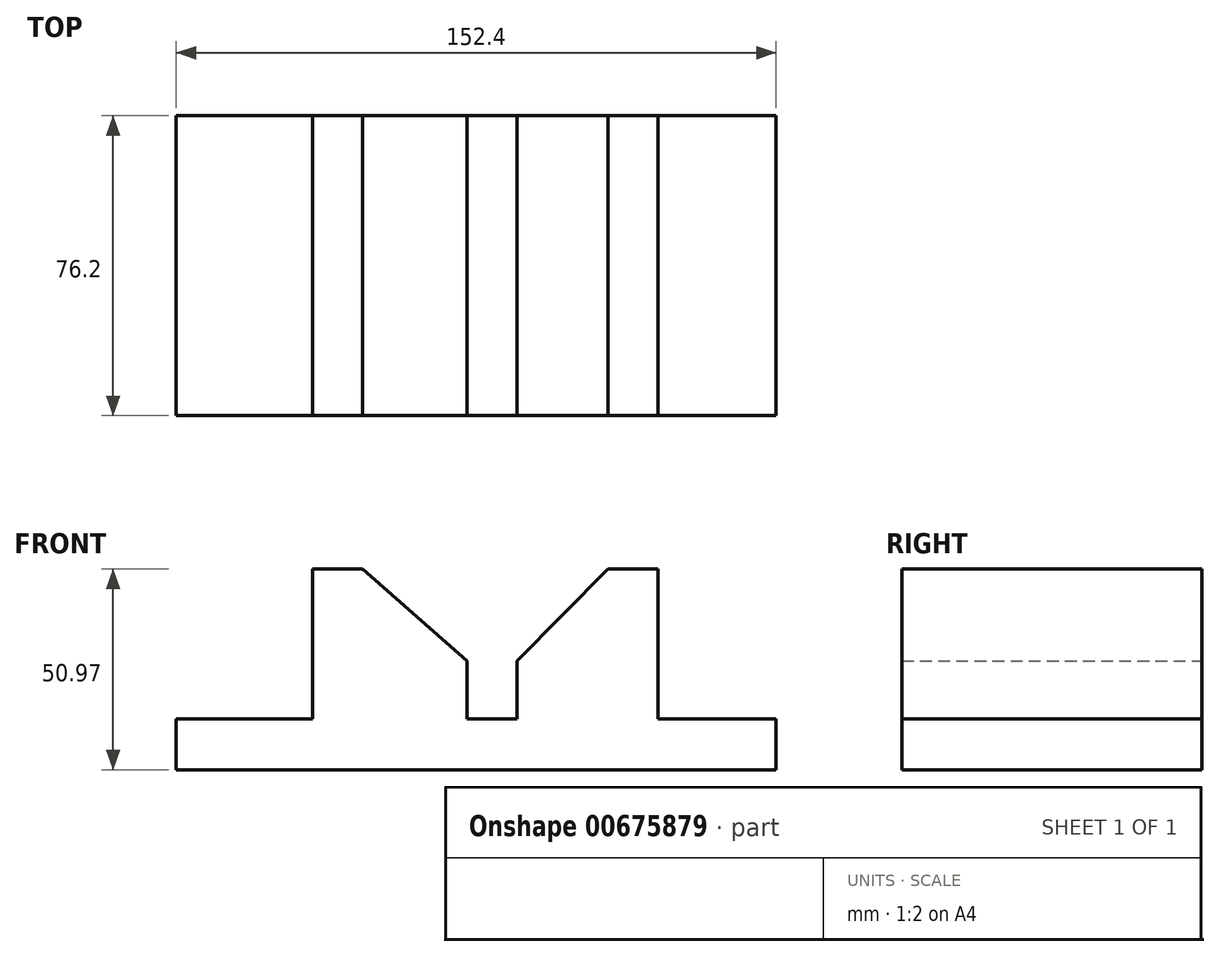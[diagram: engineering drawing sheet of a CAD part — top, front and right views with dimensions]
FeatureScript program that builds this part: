
annotation { "Feature Type Name" : "Feature", "Feature Type Description" : "" }
export const myFeature = defineFeature(function(context is Context, id is Id, definition is map)
    precondition{}
    {
        {
            var Q0;
            Q0=qCreatedBy(makeId("Front.planeOp"),FACE);
            var sketch = newSketch(context, id + "F0", { "sketchPlane" : qUnion([Q0])});
            skLineSegment(sketch, "E0", {"start": v(-79.05, 8) * mm, "end": v(-79.05, 20.7) * mm});
            skLineSegment(sketch, "E1", {"start": v(-79.05, 20.7) * mm, "end": v(-44.4, 20.7) * mm});
            skLineSegment(sketch, "E2", {"start": v(-44.4, 20.7) * mm, "end": v(-44.4, 58.8) * mm});
            skLineSegment(sketch, "E3", {"start": v(-44.4, 58.8) * mm, "end": v(-31.7, 58.8) * mm});
            skLineSegment(sketch, "E4", {"start": v(-31.7, 58.8) * mm, "end": v(-5.22, 35.5) * mm});
            skLineSegment(sketch, "E5", {"start": v(-5.22, 35.5) * mm, "end": v(-5.22, 20.7) * mm});
            skLineSegment(sketch, "E6", {"start": v(-5.22, 20.7) * mm, "end": v(7.48, 20.7) * mm});
            skLineSegment(sketch, "E7", {"start": v(7.48, 20.7) * mm, "end": v(7.48, 35.5) * mm});
            skLineSegment(sketch, "E8", {"start": v(7.48, 35.5) * mm, "end": v(30.63, 58.8) * mm});
            skLineSegment(sketch, "E9", {"start": v(30.63, 58.8) * mm, "end": v(43.33, 58.8) * mm});
            skLineSegment(sketch, "E10", {"start": v(43.33, 58.8) * mm, "end": v(43.33, 20.7) * mm});
            skLineSegment(sketch, "E11", {"start": v(43.33, 20.7) * mm, "end": v(73.35, 20.7) * mm});
            skLineSegment(sketch, "E12", {"start": v(73.35, 20.7) * mm, "end": v(73.35, 7.83) * mm});
            skLineSegment(sketch, "E13", {"start": v(73.35, 7.83) * mm, "end": v(-79.05, 7.83) * mm});
            skLineSegment(sketch, "E14", {"start": v(-79.05, 7.83) * mm, "end": v(-79.05, 8) * mm});
            skSolve(sketch);
        }
        {
            var Q0;
            Q0 = qSketchRegion(id + "F0", true);
            extrude(context, id + "F1", {"entities" : qUnion([Q0]), "depth" : 76.2 * mm, "offsetDistance" : 25.4 * mm});
        }
    });
